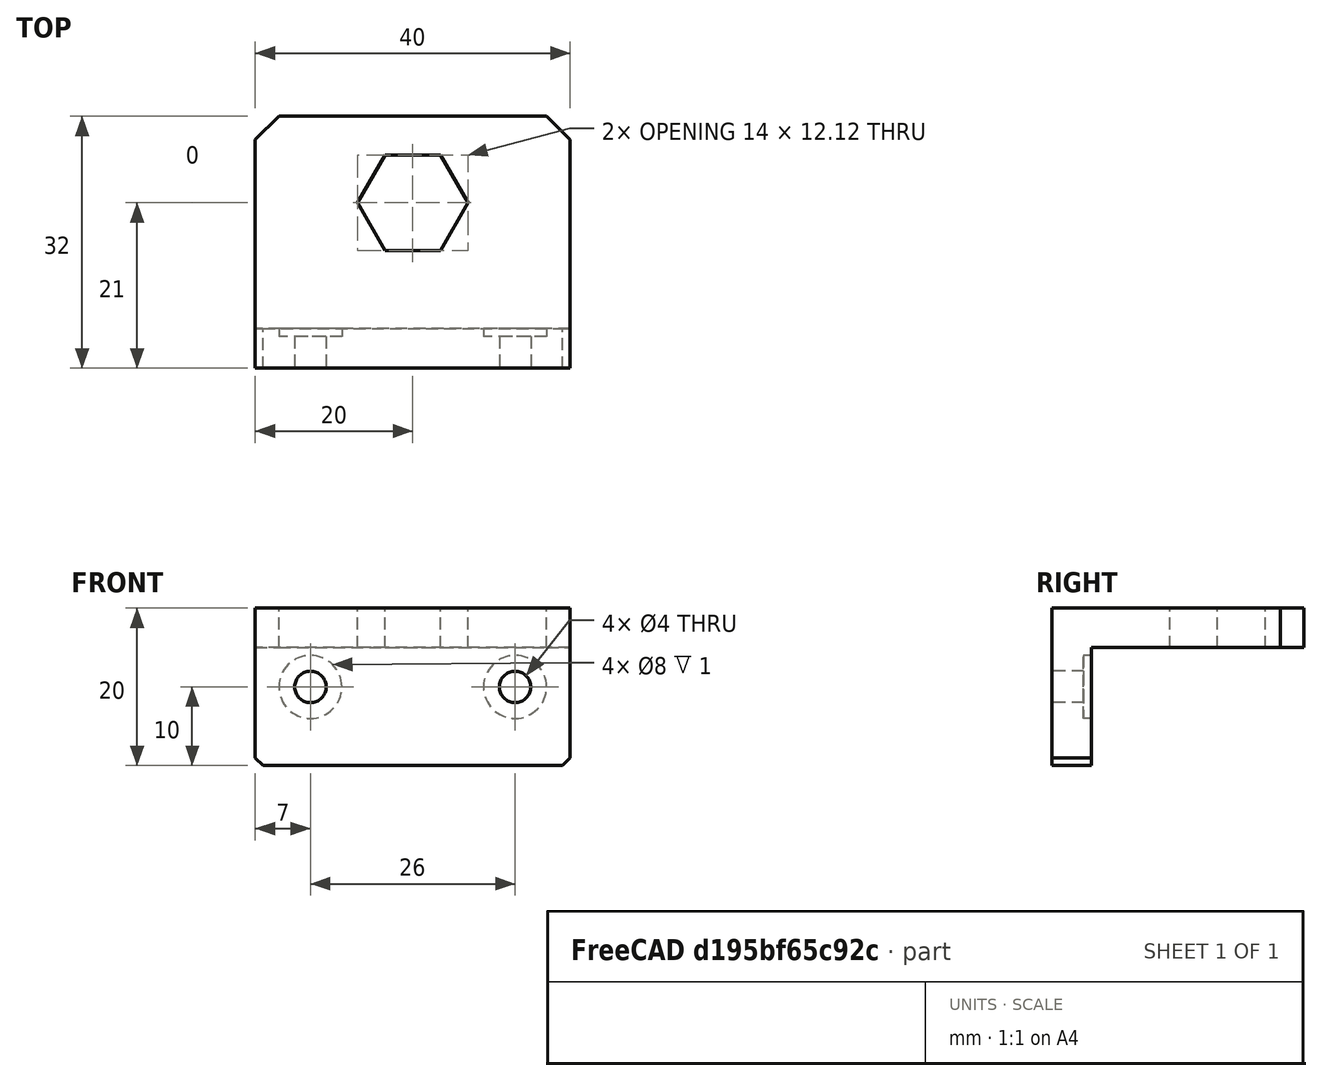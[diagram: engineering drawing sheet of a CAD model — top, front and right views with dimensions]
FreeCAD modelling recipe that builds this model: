
FCSTD DOCUMENT  (FreeCAD 0.18R14555 (Git shallow))
Label: dummy-z-top
License: All rights reserved
LicenseURL: http://en.wikipedia.org/wiki/All_rights_reserved
objects: Part::Cylinder×4, Part::MultiFuse×4, Part::Feature×3, Part::Box×2, Part::Cut×2, Part::Chamfer×2
note: 17 computed .brp shape members not serialized (recipe doc carries the construction recipe); baked Part::Feature solids carry a one-line shape summary decoded from their .brp

FEATURE [Part::Box] Box001  label="Cube001"
  AttacherType = Attacher::AttachEngine3D
  Height = 20
  Length = 40
  Width = 5
FEATURE [Part::Cylinder] Cylinder
  Angle = 360
  AttacherType = Attacher::AttachEngine3D
  Height = 1
  Placement = pos=(7,10,10) rot=(1,0,0;1.5708rad)
  Radius = 4
FEATURE [Part::Cylinder] Cylinder001
  Angle = 360
  AttacherType = Attacher::AttachEngine3D
  Height = 1
  Placement = pos=(33,10,10) rot=(1,0,0;1.5708rad)
  Radius = 4
FEATURE [Part::Cylinder] Cylinder002
  Angle = 360
  AttacherType = Attacher::AttachEngine3D
  Height = 10
  Placement = pos=(33,10,10) rot=(1,0,0;1.5708rad)
  Radius = 2
FEATURE [Part::Cylinder] Cylinder003
  Angle = 360
  AttacherType = Attacher::AttachEngine3D
  Height = 10
  Placement = pos=(7,10,10) rot=(1,0,0;1.5708rad)
  Radius = 2
FEATURE [Part::Box] Box002  label="Cube002"
  AttacherType = Attacher::AttachEngine3D
  Height = 5
  Length = 40
  Placement = pos=(0,0,15) rot=(0,0,1;0rad)
  Width = 32
FEATURE [Part::MultiFuse] Fusion
  Shapes = -> [Box002,Box001]
FEATURE [Part::MultiFuse] Fusion001
  Shapes = -> [Cylinder003,Cylinder002]
FEATURE [Part::MultiFuse] Fusion002
  Placement = pos=(0,-5,0) rot=(0,0,1;0rad)
  Shapes = -> [Cylinder,Cylinder001]
FEATURE [Part::MultiFuse] Fusion003
  Shapes = -> [Fusion001,Fusion002]
FEATURE [Part::Cut] Cut
  Base = -> Fusion
  Tool = -> Fusion003
FEATURE [Part::Feature] Body001
  Placement = pos=(60,21,0) rot=(0,0,1;0rad)
  shape: bbox 14 x 12.12 x 20 mm, 8 faces (baked)
FEATURE [Part::Cut] Cut001
  Base = -> Cut
  Tool = -> Body001
FEATURE [Part::Chamfer] Chamfer
  Base = -> Cut001
  Edges = 2 edges r=3: [Edge11,Edge31]
FEATURE [Part::Chamfer] Chamfer001
  Base = -> Chamfer
  Edges = 2 edges r=1: [Edge46,Edge56]
FEATURE [Part::Feature] Chamfer001001  label="Chamfer002"
  shape: bbox 40 x 32 x 20 mm, 24 faces (baked)
FEATURE [Part::Feature] Chamfer001001_solid  label="Chamfer002 (Solid)"
  shape: bbox 40 x 32 x 20 mm, 24 faces (baked)
